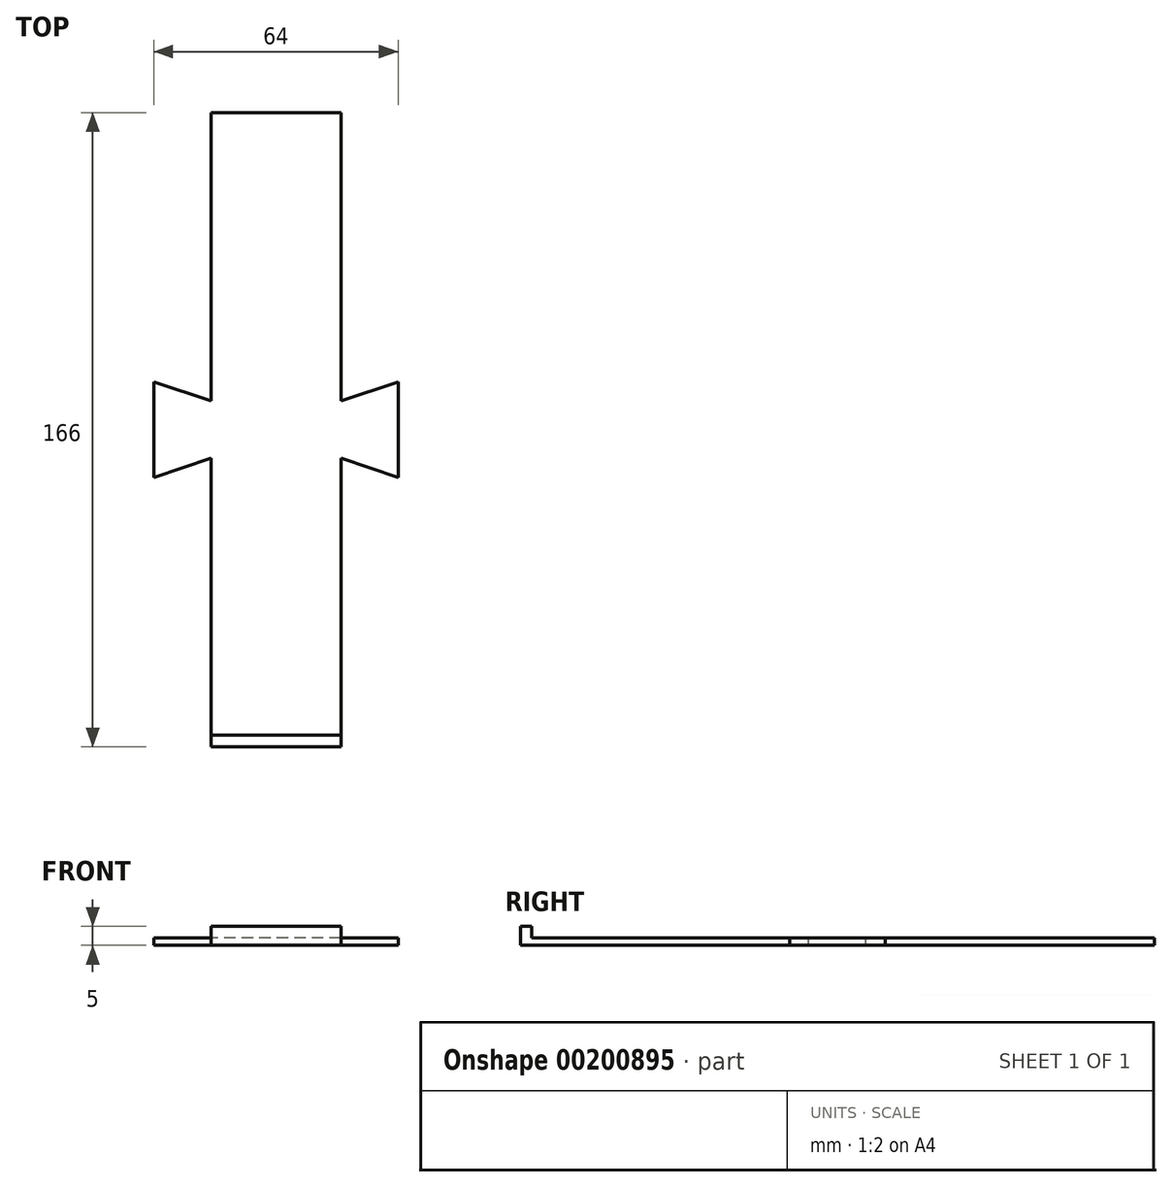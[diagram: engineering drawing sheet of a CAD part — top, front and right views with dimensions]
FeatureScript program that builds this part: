
annotation { "Feature Type Name" : "Feature", "Feature Type Description" : "" }
export const myFeature = defineFeature(function(context is Context, id is Id, definition is map)
    precondition{}
    {
        {
            var Q0;
            Q0=qCreatedBy(makeId("Top.planeOp"),FACE);
            var sketch = newSketch(context, id + "F0", { "sketchPlane" : qUnion([Q0])});
            skLineSegment(sketch, "E0.bottom", {"start": v(180, 180) * mm, "end": v(-180, 180) * mm});
            skLineSegment(sketch, "E0.top", {"start": v(180, -180) * mm, "end": v(-180, -180) * mm});
            skLineSegment(sketch, "E0.left", {"start": v(180, 180) * mm, "end": v(180, -180) * mm});
            skLineSegment(sketch, "E0.right", {"start": v(-180, 180) * mm, "end": v(-180, -180) * mm});
            skPoint(sketch, "E0.middle", {"position": v(0, 0) * mm});
            skLineSegment(sketch, "E1.bottom", {"start": v(183, 183) * mm, "end": v(-183, 183) * mm});
            skLineSegment(sketch, "E1.top", {"start": v(183, -183) * mm, "end": v(-183, -183) * mm});
            skLineSegment(sketch, "E1.left", {"start": v(183, 183) * mm, "end": v(183, -183) * mm});
            skLineSegment(sketch, "E1.right", {"start": v(-183, 183) * mm, "end": v(-183, -183) * mm});
            skSolve(sketch);
        }
        {
            var Q0;
            Q0=makeQuery(id+"F0.imprint","IMPRINT",FACE,{"disambiguationData":[TD([[makeQuery(id+"F0.imprint","IMPRINT",EDGE,{"derivedFrom":sQuery(id+"F0.wireOp",EDGE,"E0.bottom")}),1.0]])]});
            extrude(context, id + "F1", {"entities" : qUnion([Q0]), "depth" : 2 * mm});
        }
        {
            var Q0;
            Q0=makeQuery(id+"F0.imprint","IMPRINT",FACE,{"disambiguationData":[TD([[makeQuery(id+"F0.imprint","IMPRINT",EDGE,{"derivedFrom":sQuery(id+"F0.wireOp",EDGE,"E0.bottom")}),-1.0]])]});
            extrude(context, id + "F2", {"entities" : qUnion([Q0]), "operationType" : NewBodyOperationType.ADD, "depth" : 5 * mm});
        }
        {
            var Q0;
            Q0=makeQuery(id+"F2.opExtrude","CAP_FACE",FACE,{"disambiguationData":[OSD([sQuery(id+"F0.wireOp",EDGE,"E0.bottom"),sQuery(id+"F0.wireOp",EDGE,"E0.top"),sQuery(id+"F0.wireOp",EDGE,"E0.left"),sQuery(id+"F0.wireOp",EDGE,"E0.right"),sQuery(id+"F0.wireOp",EDGE,"E1.bottom"),sQuery(id+"F0.wireOp",EDGE,"E1.top"),sQuery(id+"F0.wireOp",EDGE,"E1.left"),sQuery(id+"F0.wireOp",EDGE,"E1.right")])],"isStart":false});
            var sketch = newSketch(context, id + "F3", { "sketchPlane" : qUnion([Q0])});
            skLineSegment(sketch, "E2", {"start": v(0, 0) * mm, "end": v(0, 194.54) * mm, "construction": true});
            skPoint(sketch, "E2.endSnap0", {"position": v(0, 183) * mm});
            skLineSegment(sketch, "E3", {"start": v(0, 194.54) * mm, "end": v(0, 0) * mm, "construction": true});
            skLineSegment(sketch, "E4", {"start": v(220.84, 0) * mm, "end": v(0, 0) * mm, "construction": true});
            skLineSegment(sketch, "E5.bottom", {"start": v(17, -17) * mm, "end": v(-92.5, -17) * mm});
            skLineSegment(sketch, "E5.top", {"start": v(17, 183) * mm, "end": v(-183, 183) * mm});
            skLineSegment(sketch, "E5.left", {"start": v(17, -17) * mm, "end": v(17, 92.5) * mm});
            skLineSegment(sketch, "E5.right", {"start": v(-183, -17) * mm, "end": v(-183, 183) * mm});
            skPoint(sketch, "E5.middle", {"position": v(-83, 83) * mm});
            skLineSegment(sketch, "E6.MirrorCS", {"start": v(-17, -17) * mm, "end": v(-17, 92.5) * mm});
            skLineSegment(sketch, "E7.MirrorCS", {"start": v(17, 17) * mm, "end": v(-92.5, 17) * mm});
            skLineSegment(sketch, "E8", {"start": v(-17, 17) * mm, "end": v(-17, 92.5) * mm, "construction": true});
            skLineSegment(sketch, "E9", {"start": v(-17, 100) * mm, "end": v(-183, 100) * mm, "construction": true});
            skLineSegment(sketch, "E10", {"start": v(-100, 17) * mm, "end": v(-100, 183) * mm, "construction": true});
            skLineSegment(sketch, "E11", {"start": v(-32, 87.5) * mm, "end": v(-32, 112.5) * mm});
            skLineSegment(sketch, "E12", {"start": v(-17, 92.5) * mm, "end": v(-32, 87.5) * mm});
            skLineSegment(sketch, "E13.MirrorCS", {"start": v(-17, 107.5) * mm, "end": v(-32, 112.5) * mm});
            skLineSegment(sketch, "E14.MirrorCS", {"start": v(17, 92.5) * mm, "end": v(32, 87.5) * mm});
            skLineSegment(sketch, "E15.MirrorCS", {"start": v(32, 87.5) * mm, "end": v(32, 112.5) * mm});
            skLineSegment(sketch, "E16.MirrorCS", {"start": v(17, 107.5) * mm, "end": v(32, 112.5) * mm});
            skLineSegment(sketch, "E17.trimOffspring", {"start": v(17, 107.5) * mm, "end": v(17, 183) * mm});
            skLineSegment(sketch, "E18.trimOffspring", {"start": v(-17, 107.5) * mm, "end": v(-17, 183) * mm, "construction": true});
            skLineSegment(sketch, "E19.trimOffspring", {"start": v(-17, 107.5) * mm, "end": v(-17, 183) * mm});
            skLineSegment(sketch, "E20.1.0", {"start": v(17, 17) * mm, "end": v(92.5, 17) * mm, "construction": true});
            skLineSegment(sketch, "E20.1.2", {"start": v(17, 17) * mm, "end": v(17, 92.5) * mm, "construction": true});
            skLineSegment(sketch, "E20.1.5", {"start": v(107.5, 17) * mm, "end": v(112.5, 32) * mm});
            skPoint(sketch, "E20.1.6", {"position": v(83, 83) * mm});
            skLineSegment(sketch, "E20.1.7", {"start": v(-17, 17) * mm, "end": v(92.5, 17) * mm});
            skLineSegment(sketch, "E20.1.8", {"start": v(107.5, -17) * mm, "end": v(112.5, -32) * mm});
            skLineSegment(sketch, "E20.1.9", {"start": v(92.5, -17) * mm, "end": v(87.5, -32) * mm});
            skLineSegment(sketch, "E20.1.10", {"start": v(87.5, -32) * mm, "end": v(112.5, -32) * mm});
            skLineSegment(sketch, "E20.1.11", {"start": v(107.5, 17) * mm, "end": v(183, 17) * mm, "construction": true});
            skLineSegment(sketch, "E20.1.12", {"start": v(92.5, 17) * mm, "end": v(87.5, 32) * mm});
            skLineSegment(sketch, "E20.1.13", {"start": v(-17, -17) * mm, "end": v(92.5, -17) * mm});
            skLineSegment(sketch, "E20.1.14", {"start": v(87.5, 32) * mm, "end": v(112.5, 32) * mm});
            skLineSegment(sketch, "E20.1.16", {"start": v(107.5, -17) * mm, "end": v(183, -17) * mm});
            skLineSegment(sketch, "E20.1.18", {"start": v(107.5, 17) * mm, "end": v(183, 17) * mm});
            skLineSegment(sketch, "E20.2.0", {"start": v(17, -17) * mm, "end": v(17, -92.5) * mm, "construction": true});
            skLineSegment(sketch, "E20.2.5", {"start": v(17, -107.5) * mm, "end": v(32, -112.5) * mm});
            skPoint(sketch, "E20.2.6", {"position": v(83, -83) * mm});
            skLineSegment(sketch, "E20.2.7", {"start": v(17, 17) * mm, "end": v(17, -92.5) * mm});
            skLineSegment(sketch, "E20.2.8", {"start": v(-17, -107.5) * mm, "end": v(-32, -112.5) * mm});
            skLineSegment(sketch, "E20.2.9", {"start": v(-17, -92.5) * mm, "end": v(-32, -87.5) * mm});
            skLineSegment(sketch, "E20.2.10", {"start": v(-32, -87.5) * mm, "end": v(-32, -112.5) * mm});
            skLineSegment(sketch, "E20.2.11", {"start": v(17, -107.5) * mm, "end": v(17, -183) * mm, "construction": true});
            skLineSegment(sketch, "E20.2.12", {"start": v(17, -92.5) * mm, "end": v(32, -87.5) * mm});
            skLineSegment(sketch, "E20.2.13", {"start": v(-17, 17) * mm, "end": v(-17, -92.5) * mm});
            skLineSegment(sketch, "E20.2.14", {"start": v(32, -87.5) * mm, "end": v(32, -112.5) * mm});
            skLineSegment(sketch, "E20.2.15", {"start": v(-17, -17) * mm, "end": v(92.5, -17) * mm});
            skLineSegment(sketch, "E20.2.16", {"start": v(-17, -107.5) * mm, "end": v(-17, -183) * mm});
            skLineSegment(sketch, "E20.2.18", {"start": v(17, -107.5) * mm, "end": v(17, -183) * mm});
            skPoint(sketch, "E20.center", {"position": v(0, 0) * mm});
            skLineSegment(sketch, "E21.trimOffspring", {"start": v(107.5, -17) * mm, "end": v(183, -17) * mm, "construction": true});
            skLineSegment(sketch, "E22.trimOffspring", {"start": v(17, 107.5) * mm, "end": v(17, 183) * mm, "construction": true});
            skLineSegment(sketch, "E23.MirrorCS", {"start": v(-107.5, 17) * mm, "end": v(-112.5, 32) * mm});
            skLineSegment(sketch, "E24.MirrorCS", {"start": v(-87.5, 32) * mm, "end": v(-112.5, 32) * mm});
            skLineSegment(sketch, "E25.MirrorCS", {"start": v(-92.5, 17) * mm, "end": v(-87.5, 32) * mm});
            skLineSegment(sketch, "E26.MirrorCS", {"start": v(-92.5, -17) * mm, "end": v(-87.5, -32) * mm});
            skLineSegment(sketch, "E27.MirrorCS", {"start": v(-87.5, -32) * mm, "end": v(-112.5, -32) * mm});
            skLineSegment(sketch, "E28.MirrorCS", {"start": v(-107.5, -17) * mm, "end": v(-112.5, -32) * mm});
            skLineSegment(sketch, "E29.trimOffspring", {"start": v(-107.5, -17) * mm, "end": v(-183, -17) * mm});
            skLineSegment(sketch, "E30.trimOffspring", {"start": v(-100, 17) * mm, "end": v(-183, 17) * mm, "construction": true});
            skLineSegment(sketch, "E31.trimOffspring", {"start": v(-100, 17) * mm, "end": v(-183, 17) * mm});
            skLineSegment(sketch, "E32", {"start": v(-183, -17) * mm, "end": v(17, -17) * mm, "construction": true});
            skSolve(sketch);
        }
        {
            var Q0;
            {var subQ8=sQuery(id+"F3.wireOp",EDGE,"E20.2.5");Q0=makeQuery(id+"F3.imprint","IMPRINT",FACE,{"disambiguationData":[TD([[makeQuery(id+"F3.imprint","IMPRINT",EDGE,{"derivedFrom":subQ8}),1.0]])]});}
            var Q1;
            {var subQ0=sQuery(id+"F3.wireOp",EDGE,"E20.2.16");var subQ1=makeQuery(id+"F2.opExtrude","CAP_EDGE",EDGE,{"disambiguationData":[OSD([sQuery(id+"F0.wireOp",EDGE,"E1.top")])],"isStart":false});var subQ2=makeQuery(id+"F3.imprint","INTERSECT",VERTEX,{"derivedFrom":[subQ1,subQ0]});Q1=makeQuery(id+"F3.imprint","IMPRINT",FACE,{"disambiguationData":[TD([[makeQuery(id+"F3.imprint","IMPRINT",EDGE,{"disambiguationData":[TD([[subQ2,1.0]])],"derivedFrom":subQ0}),1.0]])]});}
            extrude(context, id + "F4", {"entities" : qUnion([Q0, Q1]), "operationType" : NewBodyOperationType.INTERSECT, "oppositeDirection" : true, "depth" : 25 * mm});
        }
    });
